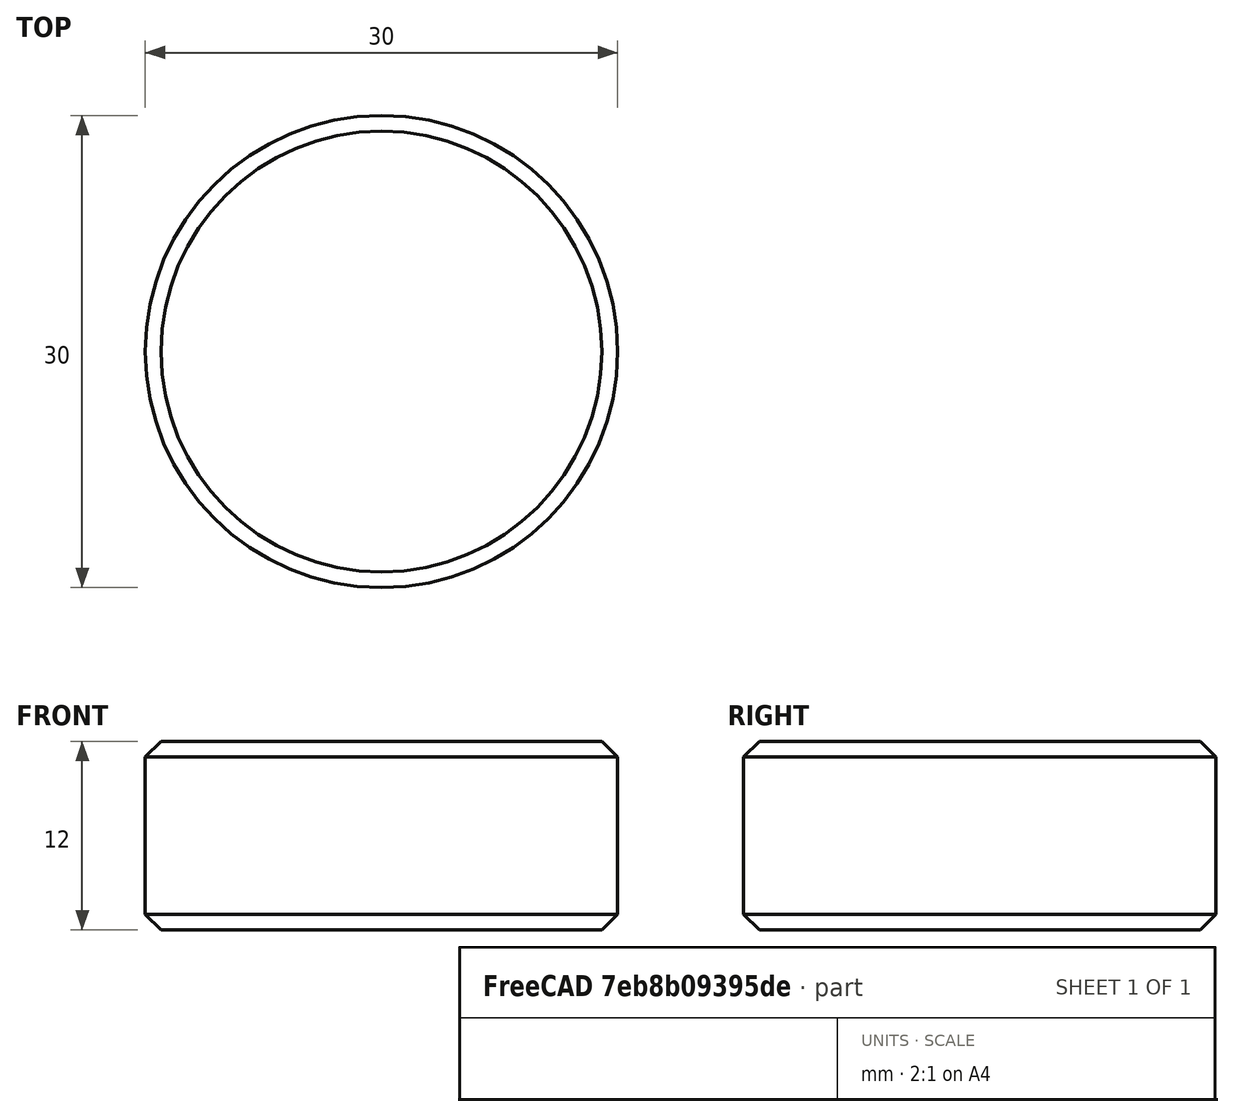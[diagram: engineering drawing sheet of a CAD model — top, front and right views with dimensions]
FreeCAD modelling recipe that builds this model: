
FCSTD DOCUMENT  (FreeCAD 1.0R39109 (Git))
Label: Puck
License: All rights reserved
LicenseURL: https://en.wikipedia.org/wiki/All_rights_reserved
objects: Sketcher::SketchObject×1, PartDesign::Pad×1, PartDesign::Chamfer×1, PartDesign::Body×1
note: 9 computed .brp shape members not serialized (recipe doc carries the construction recipe); baked Part::Feature solids carry a one-line shape summary decoded from their .brp

FEATURE [Sketcher::SketchObject] Sketch
  ArcFitTolerance = 1e-06
  AttachmentSupport = -> [XY_Plane]
  FullyConstrained = true
  MakeInternals = false
  MapMode = 5
  sketch-geometry (1):
    g0: Circle CenterX=0 CenterY=0 CenterZ=0 NormalX=0 NormalY=0 NormalZ=1 AngleXU=0 Radius=15
  constraints (2):
    c: Diameter(g0) = 30
    c: Coincident(g0,g-1)
FEATURE [PartDesign::Pad] Pad
  Direction = (0,0,1)
  Length = 12
  Length2 = 10
  Profile = -> Sketch
  ReferenceAxis = -> Sketch [N_Axis]
  Refine = true
  Suppressed = false
  Type = 0
FEATURE [PartDesign::Chamfer] Chamfer
  Angle = 45
  Base = -> Pad [Edge3,Edge2]
  BaseFeature = -> Pad
  ChamferType = 0
  FlipDirection = false
  Refine = true
  Size = 1
  Size2 = 1
  SupportTransform = false
  Suppressed = false
  UseAllEdges = false
FEATURE [PartDesign::Body] Body
  AllowCompound = false
  Group = -> [Sketch,Pad,Chamfer]
  Origin = -> Origin
  Tip = -> Chamfer
